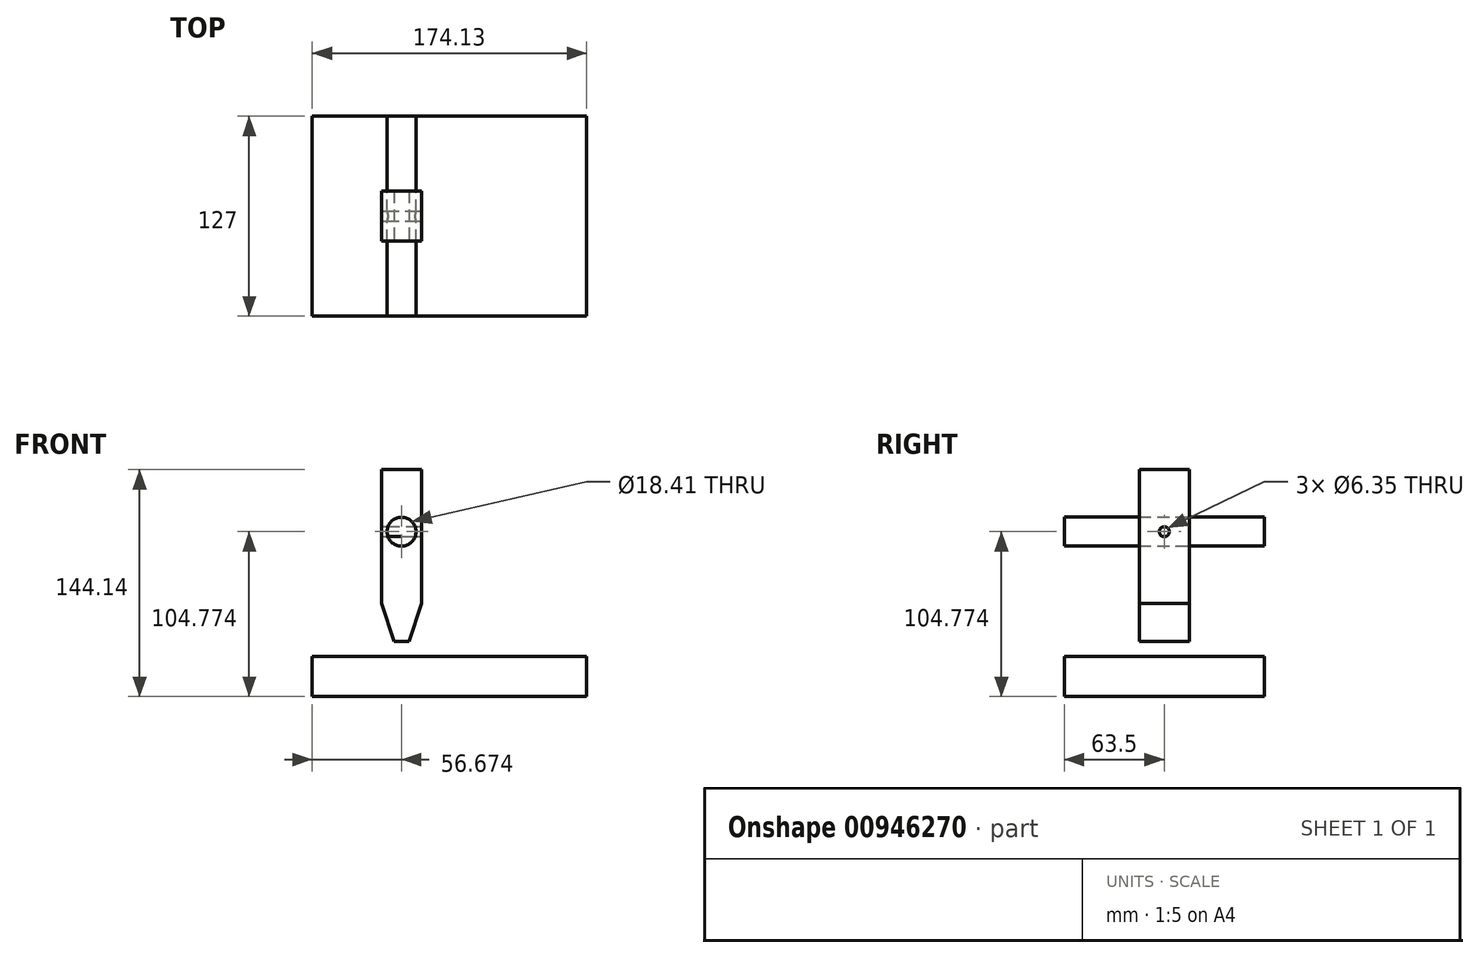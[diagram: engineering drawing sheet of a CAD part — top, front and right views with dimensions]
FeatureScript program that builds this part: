
annotation { "Feature Type Name" : "Feature", "Feature Type Description" : "" }
export const myFeature = defineFeature(function(context is Context, id is Id, definition is map)
    precondition{}
    {
        {
            var Q0;
            Q0=qCreatedBy(makeId("Front.planeOp"),FACE);
            var sketch = newSketch(context, id + "F0", { "sketchPlane" : qUnion([Q0])});
            skCircle(sketch, "E0", {"center": v(9.52, 89.46) * mm, "radius": 9.2 * mm});
            skLineSegment(sketch, "E1", {"start": v(9.52, 89.46) * mm, "end": v(9.52, 10.09) * mm});
            skLineSegment(sketch, "E2.bottom", {"start": v(-47.15, 10.09) * mm, "end": v(126.98, 10.09) * mm});
            skLineSegment(sketch, "E2.top", {"start": v(-47.15, -15.3) * mm, "end": v(126.98, -15.3) * mm});
            skLineSegment(sketch, "E2.left", {"start": v(-47.15, 10.09) * mm, "end": v(-47.15, -15.3) * mm});
            skLineSegment(sketch, "E2.right", {"start": v(126.98, 10.09) * mm, "end": v(126.98, -15.3) * mm});
            skSolve(sketch);
        }
        {
            var Q0;
            Q0 = qSketchRegion(id + "F0", true);
            extrude(context, id + "F1", {"entities" : qUnion([Q0]), "depth" : 127 * mm, "offsetDistance" : 25.4 * mm, "symmetric" : true});
        }
        {
            var Q0;
            Q0=qCreatedBy(makeId("Front.planeOp"),FACE);
            var sketch = newSketch(context, id + "F2", { "sketchPlane" : qUnion([Q0])});
            skLineSegment(sketch, "E3", {"start": v(22.23, 128.83) * mm, "end": v(22.23, 19.61) * mm});
            skLineSegment(sketch, "E4", {"start": v(22.23, 19.61) * mm, "end": v(9.53, 19.61) * mm});
            skLineSegment(sketch, "E5", {"start": v(22.23, 128.83) * mm, "end": v(9.53, 128.83) * mm});
            skLineSegment(sketch, "E6", {"start": v(9.52, 128.83) * mm, "end": v(-3.18, 128.83) * mm});
            skCircle(sketch, "E7.0.0", {"center": v(9.52, 89.46) * mm, "radius": 9.2 * mm});
            skLineSegment(sketch, "E8", {"start": v(-3.18, 128.83) * mm, "end": v(-3.18, 19.61) * mm});
            skLineSegment(sketch, "E9", {"start": v(-3.18, 19.61) * mm, "end": v(9.53, 19.61) * mm});
            skSolve(sketch);
        }
        {
            var Q0;
            Q0 = qSketchRegion(id + "F2", true);
            extrude(context, id + "F3", {"entities" : qUnion([Q0]), "depth" : 31.75 * mm, "offsetDistance" : 25.4 * mm, "symmetric" : true});
        }
        {
            var Q0;
            Q0=makeQuery(id+"F3.opExtrude","CAP_FACE",FACE,{"disambiguationData":[OSD([sQuery(id+"F2.wireOp",EDGE,"E3"),sQuery(id+"F2.wireOp",EDGE,"E4"),sQuery(id+"F2.wireOp",EDGE,"E5"),sQuery(id+"F2.wireOp",EDGE,"E6"),sQuery(id+"F2.wireOp",EDGE,"N425rXRN-eGfM-iy2G-zD17-O8afRylmF3nQ"),sQuery(id+"F2.wireOp",EDGE,"2b4wmNuW-PuKU-8UHR-sF1A-5k6suPvKTMbE"),sQuery(id+"F2.wireOp",EDGE,"E7.0.0")])],"isStart":false});
            var sketch = newSketch(context, id + "F4", { "sketchPlane" : qUnion([Q0])});
            skLineSegment(sketch, "E10", {"start": v(9.53, 19.61) * mm, "end": v(4.76, 19.61) * mm});
            skLineSegment(sketch, "E11", {"start": v(9.53, 19.61) * mm, "end": v(14.29, 19.61) * mm});
            skLineSegment(sketch, "E12", {"start": v(4.76, 19.61) * mm, "end": v(-3.18, 43.74) * mm});
            skLineSegment(sketch, "E13", {"start": v(22.23, 43.74) * mm, "end": v(14.29, 19.61) * mm});
            skLineSegment(sketch, "E14.0.0", {"start": v(22.23, 19.61) * mm, "end": v(22.23, 128.83) * mm});
            skLineSegment(sketch, "E14.0.1", {"start": v(22.23, 128.83) * mm, "end": v(-3.18, 128.83) * mm});
            skLineSegment(sketch, "E14.0.2", {"start": v(-3.18, 128.83) * mm, "end": v(-3.18, 19.61) * mm});
            skLineSegment(sketch, "E14.0.3", {"start": v(-3.18, 19.61) * mm, "end": v(22.23, 19.61) * mm});
            skSolve(sketch);
        }
        {
            var Q0;
            {var subQ0=sQuery(id+"F4.wireOp",EDGE,"E12");Q0=makeQuery(id+"F4.imprint","IMPRINT",FACE,{"disambiguationData":[TD([[makeQuery(id+"F4.imprint","IMPRINT",EDGE,{"derivedFrom":subQ0}),1.0]])]});}
            var Q1;
            {var subQ0=sQuery(id+"F4.wireOp",EDGE,"E13");Q1=makeQuery(id+"F4.imprint","IMPRINT",FACE,{"disambiguationData":[TD([[makeQuery(id+"F4.imprint","IMPRINT",EDGE,{"derivedFrom":subQ0}),1.0]])]});}
            extrude(context, id + "F5", {"entities" : qUnion([Q0, Q1]), "operationType" : NewBodyOperationType.REMOVE, "endBound" : BoundingType.THROUGH_ALL, "oppositeDirection" : true, "depth" : 25.4 * mm, "offsetDistance" : 25.4 * mm});
        }
        {
            var Q0;
            Q0=makeQuery(id+"F3.opExtrude","SWEPT_FACE",FACE,{"disambiguationData":[OSD([sQuery(id+"F2.wireOp",EDGE,"E3")])]});
            var sketch = newSketch(context, id + "F6", { "sketchPlane" : qUnion([Q0])});
            skLineSegment(sketch, "E15.0", {"start": v(-63.5, 80.26) * mm, "end": v(-63.5, 98.67) * mm});
            skCircle(sketch, "E16", {"center": v(0, 89.46) * mm, "radius": 3.18 * mm});
            skPoint(sketch, "E16.centerSnap0", {"position": v(-63.5, 89.46) * mm});
            skSolve(sketch);
        }
        {
            var Q0;
            Q0=makeQuery(id+"F6.imprint","IMPRINT",FACE,{"disambiguationData":[TD([[makeQuery(id+"F6.imprint","IMPRINT",EDGE,{"derivedFrom":sQuery(id+"F6.wireOp",EDGE,"E16")}),1.0]])]});
            extrude(context, id + "F7", {"entities" : qUnion([Q0]), "operationType" : NewBodyOperationType.REMOVE, "endBound" : BoundingType.THROUGH_ALL, "oppositeDirection" : true, "depth" : 25.4 * mm, "offsetDistance" : 25.4 * mm});
        }
    });
